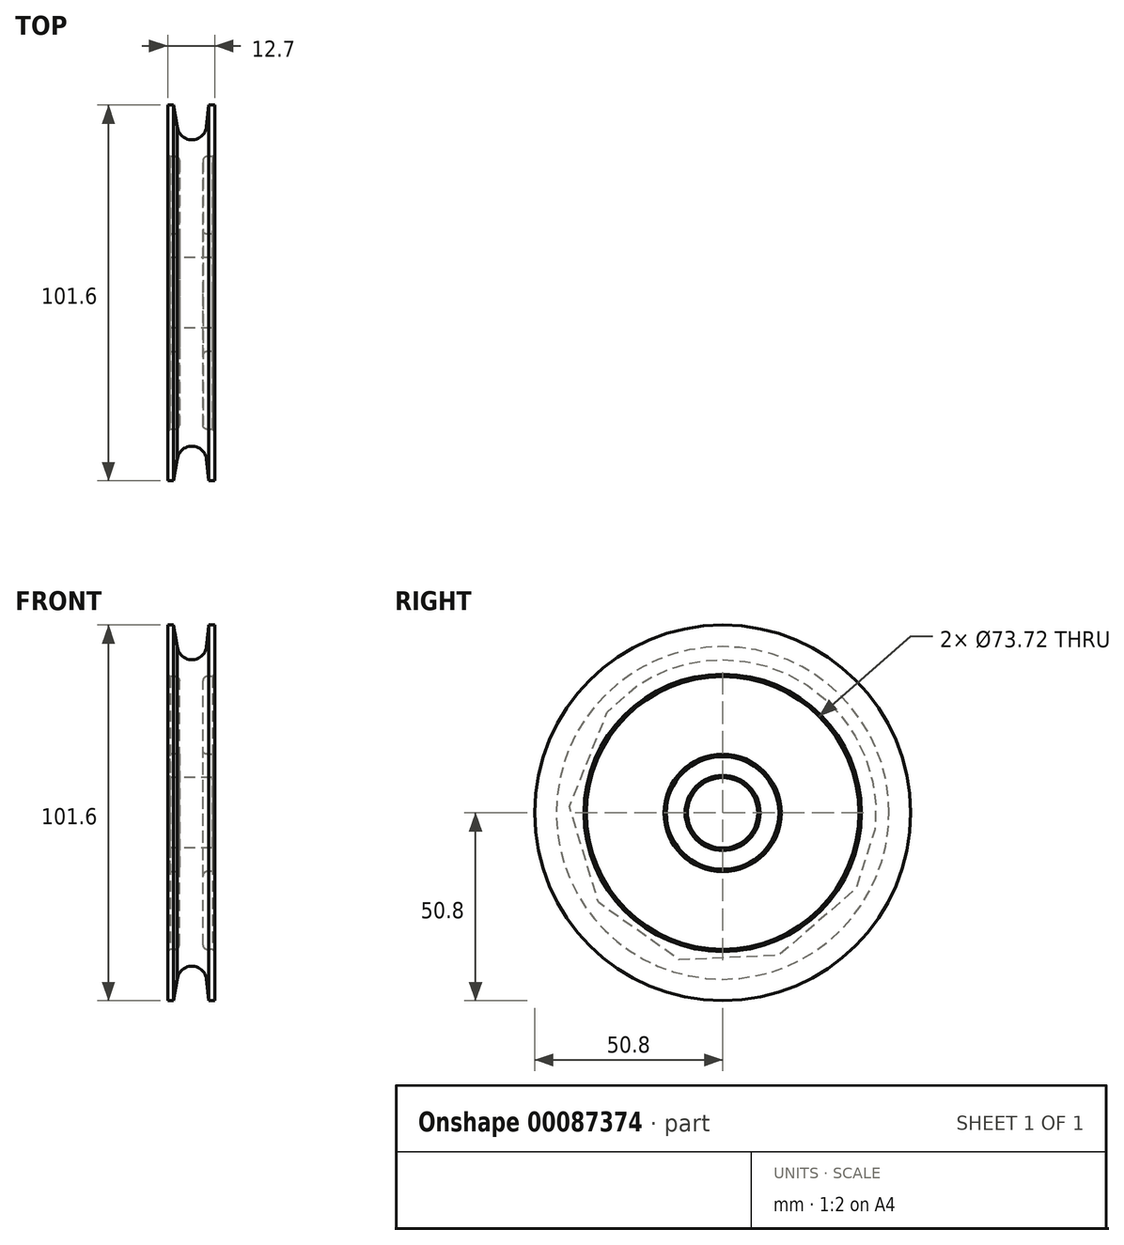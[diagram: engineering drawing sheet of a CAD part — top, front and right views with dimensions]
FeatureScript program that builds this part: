
annotation { "Feature Type Name" : "Feature", "Feature Type Description" : "" }
export const myFeature = defineFeature(function(context is Context, id is Id, definition is map)
    precondition{}
    {
        {
            var Q0;
            Q0=qCreatedBy(makeId("Front.planeOp"),FACE);
            var sketch = newSketch(context, id + "F0", { "sketchPlane" : qUnion([Q0])});
            skLineSegment(sketch, "E0", {"start": v(2.8, 47.38) * mm, "end": v(2.8, 26.42) * mm});
            skLineSegment(sketch, "E1", {"start": v(9.15, 47.38) * mm, "end": v(9.15, 26.38) * mm});
            skPoint(sketch, "E2.start.orphan", {"position": v(12.7, 0) * mm});
            skPoint(sketch, "E3.trimOffspring.end.orphan", {"position": v(0, 0) * mm});
            skLineSegment(sketch, "E4", {"start": v(0, 10.52) * mm, "end": v(15.28, 10.52) * mm, "construction": true});
            skLineSegment(sketch, "E5", {"start": v(-0.37, 20.04) * mm, "end": v(12.33, 20.03) * mm});
            skArc(sketch, "E6", {"start": v(2.22, 55.5) * mm, "mid": v(6.16, 51.94) * mm, "end": v(10.11, 55.5) * mm});
            skLineSegment(sketch, "E7", {"start": v(-0.37, 47.38) * mm, "end": v(2.8, 47.38) * mm});
            skPoint(sketch, "E8.endSnap0", {"position": v(6.16, 51.94) * mm});
            skPoint(sketch, "E9.orphan", {"position": v(2.8, 39.62) * mm});
            skPoint(sketch, "E10.orphan", {"position": v(9.15, 39.62) * mm});
            skLineSegment(sketch, "E11.trimOffspring", {"start": v(9.15, 47.38) * mm, "end": v(12.33, 47.38) * mm});
            skLineSegment(sketch, "E12", {"start": v(-0.37, 47.38) * mm, "end": v(-0.37, 61.32) * mm});
            skLineSegment(sketch, "E13", {"start": v(-0.37, 61.32) * mm, "end": v(1.2, 61.32) * mm});
            skLineSegment(sketch, "E14", {"start": v(1.2, 61.32) * mm, "end": v(2.22, 55.5) * mm});
            skLineSegment(sketch, "E15", {"start": v(12.33, 47.38) * mm, "end": v(12.33, 61.32) * mm});
            skLineSegment(sketch, "E16", {"start": v(12.33, 61.32) * mm, "end": v(10.76, 61.32) * mm});
            skLineSegment(sketch, "E17", {"start": v(10.76, 61.32) * mm, "end": v(10.11, 55.5) * mm});
            skLineSegment(sketch, "E18", {"start": v(2.8, 26.42) * mm, "end": v(-0.37, 26.42) * mm});
            skLineSegment(sketch, "E19", {"start": v(-0.37, 26.42) * mm, "end": v(-0.37, 20.04) * mm});
            skLineSegment(sketch, "E20", {"start": v(12.33, 20.03) * mm, "end": v(12.33, 26.38) * mm});
            skLineSegment(sketch, "E21", {"start": v(12.33, 26.38) * mm, "end": v(9.15, 26.38) * mm});
            skSolve(sketch);
        }
        {
            var Q0;
            Q0=makeQuery(id+"F0.imprint","IMPRINT",FACE,{"disambiguationData":[TD([[makeQuery(id+"F0.imprint","IMPRINT",EDGE,{"derivedFrom":sQuery(id+"F0.wireOp",EDGE,"E0")}),1.0]])]});
            var Q1;
            Q1=sQuery(id+"F0.wireOp",EDGE,"E4");
            revolve(context, id + "F1", {"entities" : qUnion([Q0]), "axis" : qUnion([Q1]), "revolveType" : RevolveType.FULL});
        }
        {
            var Q0;
            Q0=makeQuery(id+"F1.opRevolve","SWEPT_EDGE",EDGE,{"disambiguationData":[OSD([sQuery(id+"F0.wireOp",EDGE,"E11.trimOffspring"),sQuery(id+"F0.wireOp",EDGE,"E15")])]});
            var Q1;
            Q1=makeQuery(id+"F1.opRevolve","SWEPT_EDGE",EDGE,{"disambiguationData":[OSD([sQuery(id+"F0.wireOp",EDGE,"E20"),sQuery(id+"F0.wireOp",EDGE,"E21")])]});
            var Q2;
            Q2=makeQuery(id+"F1.opRevolve","SWEPT_EDGE",EDGE,{"disambiguationData":[OSD([sQuery(id+"F0.wireOp",EDGE,"E5"),sQuery(id+"F0.wireOp",EDGE,"E20")])]});
            var Q3;
            Q3=makeQuery(id+"F1.opRevolve","SWEPT_EDGE",EDGE,{"disambiguationData":[OSD([sQuery(id+"F0.wireOp",EDGE,"E5"),sQuery(id+"F0.wireOp",EDGE,"E19")])]});
            var Q4;
            Q4=makeQuery(id+"F1.opRevolve","SWEPT_EDGE",EDGE,{"disambiguationData":[OSD([sQuery(id+"F0.wireOp",EDGE,"E18"),sQuery(id+"F0.wireOp",EDGE,"E19")])]});
            var Q5;
            Q5=makeQuery(id+"F1.opRevolve","SWEPT_EDGE",EDGE,{"disambiguationData":[OSD([sQuery(id+"F0.wireOp",EDGE,"E7"),sQuery(id+"F0.wireOp",EDGE,"E12")])]});
            chamfer(context, id + "F2", {"entities" : qUnion([Q0, Q1, Q2, Q3, Q4, Q5]), "width" : 0.64 * mm, "tangentPropagation" : true});
        }
        {
            var Q0;
            Q0=makeQuery(id+"F1.opRevolve","SWEPT_EDGE",EDGE,{"disambiguationData":[OSD([sQuery(id+"F0.wireOp",EDGE,"E0"),sQuery(id+"F0.wireOp",EDGE,"E7")])]});
            var Q1;
            Q1=makeQuery(id+"F1.opRevolve","SWEPT_EDGE",EDGE,{"disambiguationData":[OSD([sQuery(id+"F0.wireOp",EDGE,"E1"),sQuery(id+"F0.wireOp",EDGE,"E11.trimOffspring")])]});
            var Q2;
            Q2=makeQuery(id+"F1.opRevolve","SWEPT_EDGE",EDGE,{"disambiguationData":[OSD([sQuery(id+"F0.wireOp",EDGE,"E1"),sQuery(id+"F0.wireOp",EDGE,"E21")])]});
            fillet(context, id + "F3", {"entities" : qUnion([Q0, Q1, Q2]), "radius" : 1.14 * mm, "tangentPropagation" : true, "allowEdgeOverflow" : false});
        }
    });
